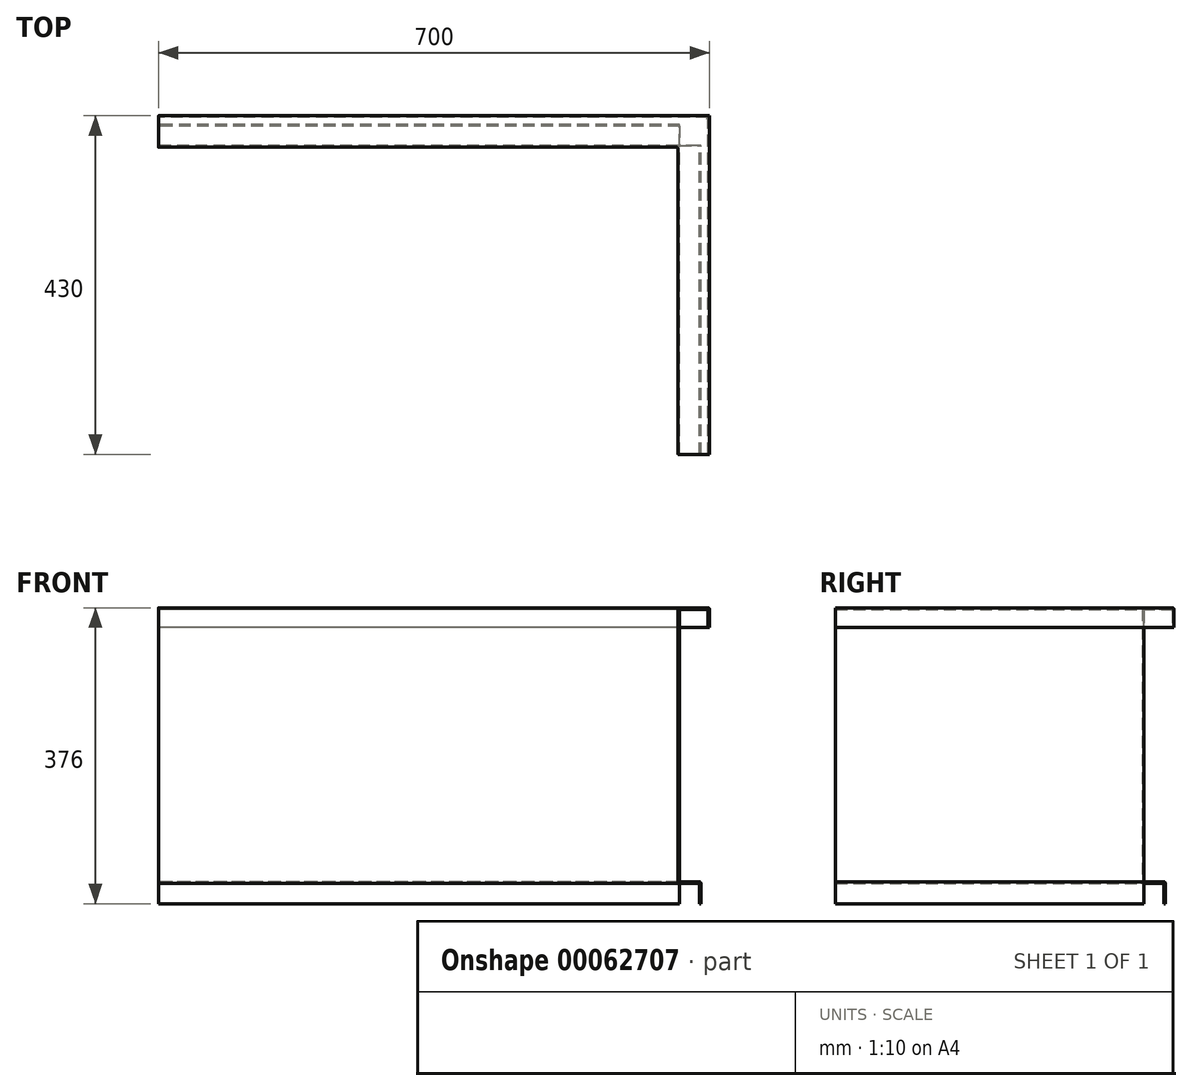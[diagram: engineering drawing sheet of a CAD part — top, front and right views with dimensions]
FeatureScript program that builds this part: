
annotation { "Feature Type Name" : "Feature", "Feature Type Description" : "" }
export const myFeature = defineFeature(function(context is Context, id is Id, definition is map)
    precondition{}
    {
        {
            var Q0;
            Q0=qCreatedBy(makeId("Front.planeOp"),FACE);
            var sketch = newSketch(context, id + "F0", { "sketchPlane" : qUnion([Q0])});
            skLineSegment(sketch, "E0", {"start": v(38, -25) * mm, "end": v(38, -2) * mm});
            skLineSegment(sketch, "E1", {"start": v(38, -2) * mm, "end": v(2, -2) * mm});
            skLineSegment(sketch, "E2", {"start": v(2, -2) * mm, "end": v(2, -348) * mm});
            skLineSegment(sketch, "E3", {"start": v(2, -348) * mm, "end": v(29, -348) * mm});
            skLineSegment(sketch, "E4", {"start": v(29, -348) * mm, "end": v(29, -376) * mm});
            skLineSegment(sketch, "E5.0", {"start": v(27, -350) * mm, "end": v(27, -376) * mm});
            skLineSegment(sketch, "E5.1", {"start": v(40, -25) * mm, "end": v(40, 0) * mm});
            skLineSegment(sketch, "E5.2", {"start": v(40, 0) * mm, "end": v(0, 0) * mm});
            skLineSegment(sketch, "E5.3", {"start": v(0, 0) * mm, "end": v(0, -350) * mm});
            skLineSegment(sketch, "E5.4", {"start": v(0, -350) * mm, "end": v(27, -350) * mm});
            skLineSegment(sketch, "E6", {"start": v(27, -376) * mm, "end": v(29, -376) * mm});
            skLineSegment(sketch, "E7", {"start": v(38, -25) * mm, "end": v(40, -25) * mm});
            skSolve(sketch);
        }
        {
            var Q0;
            Q0=qCreatedBy(makeId("Top.planeOp"),FACE);
            var sketch = newSketch(context, id + "F1", { "sketchPlane" : qUnion([Q0])});
            skLineSegment(sketch, "E8", {"start": v(0, 0) * mm, "end": v(0, 390) * mm});
            skLineSegment(sketch, "E9", {"start": v(0, 390) * mm, "end": v(-660, 390) * mm});
            skSolve(sketch);
        }
        {
            var Q0;
            Q0 = qSketchRegion(id + "F0", true);
            var Q1;
            Q1 = qConstructionFilter(qBodyType(qCreatedBy(id + "F1" ,EDGE), BodyType.WIRE), ConstructionObject.NO);
            sweep(context, id + "F2", {"profiles" : qUnion([Q0]), "path" : qUnion([Q1])});
        }
        {
            var Q0;
            Q0=makeQuery(id+"F2.opSweep","SWEPT_FACE",FACE,{"disambiguationData":[OSD([sQuery(id+"F0.wireOp",EDGE,"E3"),sQuery(id+"F1.wireOp",EDGE,"E8")])]});
            var sketch = newSketch(context, id + "F3", { "sketchPlane" : qUnion([Q0])});
            skLineSegment(sketch, "E10", {"start": v(2, 392) * mm, "end": v(29, 392) * mm});
            skLineSegment(sketch, "E11", {"start": v(29, 392) * mm, "end": v(29, 419) * mm});
            skLineSegment(sketch, "E12", {"start": v(29, 419) * mm, "end": v(2, 419) * mm});
            skLineSegment(sketch, "E13", {"start": v(2, 419) * mm, "end": v(2, 392) * mm});
            skSolve(sketch);
        }
        {
            var Q0;
            Q0 = qSketchRegion(id + "F3", true);
            extrude(context, id + "F4", {"entities" : qUnion([Q0]), "operationType" : NewBodyOperationType.REMOVE, "oppositeDirection" : true, "depth" : 30 * mm});
        }
        {
            var Q0;
            Q0=makeQuery(id+"F2.opSweep","SWEPT_EDGE",EDGE,{"disambiguationData":[OSD([sQuery(id+"F0.wireOp",EDGE,"E3"),sQuery(id+"F0.wireOp",EDGE,"E4"),sQuery(id+"F1.wireOp",EDGE,"E8")])]});
            var Q1;
            Q1=makeQuery(id+"F2.opSweep","SWEPT_EDGE",EDGE,{"disambiguationData":[OSD([sQuery(id+"F0.wireOp",EDGE,"E3"),sQuery(id+"F0.wireOp",EDGE,"E4"),sQuery(id+"F1.wireOp",EDGE,"E9")])]});
            var Q2;
            Q2=makeQuery(id+"F2.opSweep","SWEPT_EDGE",EDGE,{"disambiguationData":[OSD([sQuery(id+"F0.wireOp",EDGE,"E5.1"),sQuery(id+"F0.wireOp",EDGE,"E5.2"),sQuery(id+"F1.wireOp",EDGE,"E9")])]});
            var Q3;
            Q3=makeQuery(id+"F2.opSweep","SWEPT_EDGE",EDGE,{"disambiguationData":[OSD([sQuery(id+"F0.wireOp",EDGE,"E5.1"),sQuery(id+"F0.wireOp",EDGE,"E5.2"),sQuery(id+"F1.wireOp",EDGE,"E8")])]});
            var Q4;
            Q4=makeQuery(id+"F2.opSweep","MID_CAP_EDGE",EDGE,{"disambiguationData":[OSD([sQuery(id+"F0.wireOp",EDGE,"E2"),sQuery(id+"F1.wireOp",VERTEX,"E9.start")])],"capPos":1.0});
            var Q5;
            Q5=makeQuery(id+"F2.opSweep","SWEPT_EDGE",EDGE,{"disambiguationData":[OSD([sQuery(id+"F0.wireOp",EDGE,"E5.3"),sQuery(id+"F0.wireOp",EDGE,"E5.4"),sQuery(id+"F1.wireOp",EDGE,"E8")])]});
            var Q6;
            Q6=makeQuery(id+"F2.opSweep","SWEPT_EDGE",EDGE,{"disambiguationData":[OSD([sQuery(id+"F0.wireOp",EDGE,"E5.3"),sQuery(id+"F0.wireOp",EDGE,"E5.4"),sQuery(id+"F1.wireOp",EDGE,"E9")])]});
            var Q7;
            Q7=makeQuery(id+"F2.opSweep","SWEPT_EDGE",EDGE,{"disambiguationData":[OSD([sQuery(id+"F0.wireOp",EDGE,"E5.2"),sQuery(id+"F0.wireOp",EDGE,"E5.3"),sQuery(id+"F1.wireOp",EDGE,"E9")])]});
            var Q8;
            Q8=makeQuery(id+"F2.opSweep","SWEPT_EDGE",EDGE,{"disambiguationData":[OSD([sQuery(id+"F0.wireOp",EDGE,"E5.2"),sQuery(id+"F0.wireOp",EDGE,"E5.3"),sQuery(id+"F1.wireOp",EDGE,"E8")])]});
            var Q9;
            Q9=makeQuery(id+"F2.opSweep","SWEPT_EDGE",EDGE,{"disambiguationData":[OSD([sQuery(id+"F0.wireOp",EDGE,"E1"),sQuery(id+"F0.wireOp",EDGE,"E2"),sQuery(id+"F1.wireOp",EDGE,"E8")])]});
            var Q10;
            Q10=makeQuery(id+"F2.opSweep","SWEPT_EDGE",EDGE,{"disambiguationData":[OSD([sQuery(id+"F0.wireOp",EDGE,"E1"),sQuery(id+"F0.wireOp",EDGE,"E2"),sQuery(id+"F1.wireOp",EDGE,"E9")])]});
            var Q11;
            Q11=makeQuery(id+"F2.opSweep","SWEPT_EDGE",EDGE,{"disambiguationData":[OSD([sQuery(id+"F0.wireOp",EDGE,"E0"),sQuery(id+"F0.wireOp",EDGE,"E1"),sQuery(id+"F1.wireOp",EDGE,"E8")])]});
            var Q12;
            Q12=makeQuery(id+"F2.opSweep","SWEPT_EDGE",EDGE,{"disambiguationData":[OSD([sQuery(id+"F0.wireOp",EDGE,"E0"),sQuery(id+"F0.wireOp",EDGE,"E1"),sQuery(id+"F1.wireOp",EDGE,"E9")])]});
            var Q13;
            Q13=makeQuery(id+"F2.opSweep","SWEPT_EDGE",EDGE,{"disambiguationData":[OSD([sQuery(id+"F0.wireOp",EDGE,"E5.0"),sQuery(id+"F0.wireOp",EDGE,"E5.4"),sQuery(id+"F1.wireOp",EDGE,"E9")])]});
            var Q14;
            Q14=makeQuery(id+"F2.opSweep","SWEPT_EDGE",EDGE,{"disambiguationData":[OSD([sQuery(id+"F0.wireOp",EDGE,"E5.0"),sQuery(id+"F0.wireOp",EDGE,"E5.4"),sQuery(id+"F1.wireOp",EDGE,"E8")])]});
            var Q15;
            Q15=makeQuery(id+"F2.opSweep","MID_CAP_EDGE",EDGE,{"disambiguationData":[OSD([sQuery(id+"F0.wireOp",EDGE,"E5.3"),sQuery(id+"F1.wireOp",VERTEX,"E9.start")])],"capPos":1.0});
            fillet(context, id + "F5", {"entities" : qUnion([Q0, Q1, Q2, Q3, Q4, Q5, Q6, Q7, Q8, Q9, Q10, Q11, Q12, Q13, Q14, Q15]), "radius" : 2 * mm, "tangentPropagation" : true, "allowEdgeOverflow" : false});
        }
    });
